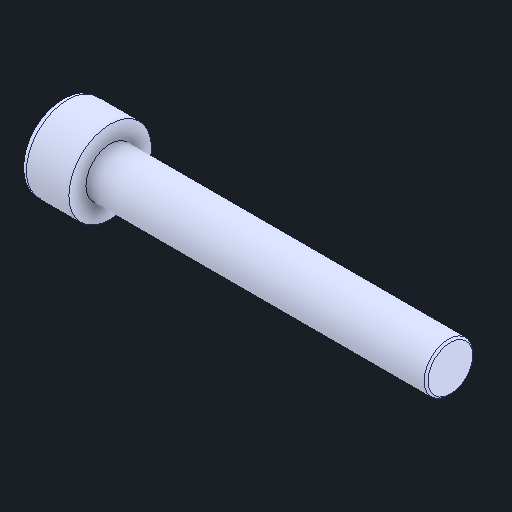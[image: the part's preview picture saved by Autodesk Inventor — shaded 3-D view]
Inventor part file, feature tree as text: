
AUTODESK INVENTOR PART (.ipt)
format: ipt  version: 2025 (Build 290162000, 162)  size: 112,640 bytes
history: native  units: mm
features: chamfer x1
ambient origin geometry x8: Origin, YZ Plane, XZ Plane, XY Plane, X Axis, Y Axis, Z Axis, Center Point
bodies: 实体1 (feature_tree)
feature tree (1):
  chamfer  "Chamfer1"  [1 undecoded]
note: 1 required parameter value undecoded (feature->parameter linkage not recoverable at this tier; creation-order binding heuristic only, values carry confidence <= 0.55)
